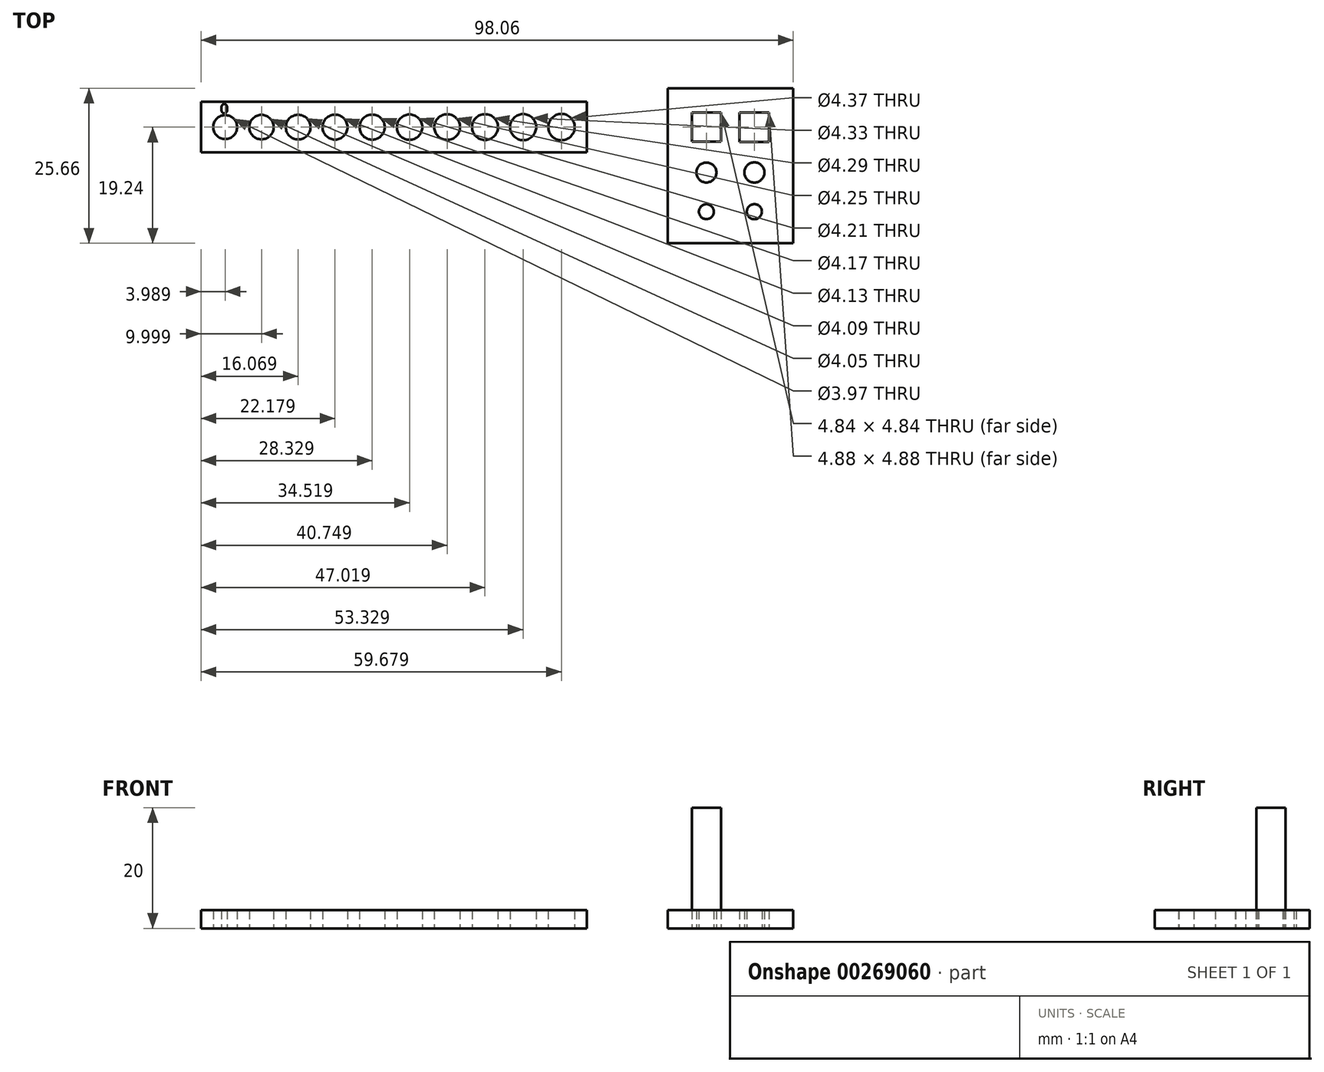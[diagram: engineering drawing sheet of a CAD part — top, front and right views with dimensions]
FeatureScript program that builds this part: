
annotation { "Feature Type Name" : "Feature", "Feature Type Description" : "" }
export const myFeature = defineFeature(function(context is Context, id is Id, definition is map)
    precondition{}
    {
        {
            var Q0;
            Q0=qCreatedBy(makeId("Top.planeOp"),FACE);
            var sketch = newSketch(context, id + "F0", { "sketchPlane" : qUnion([Q0])});
            skLineSegment(sketch, "E0", {"start": v(-79.68, 0) * mm, "end": v(-31, 0) * mm, "construction": true});
            skCircle(sketch, "E1", {"center": v(-79.68, 0) * mm, "radius": 1.99 * mm});
            skCircle(sketch, "E2", {"center": v(-73.67, 0) * mm, "radius": 2.02 * mm});
            skCircle(sketch, "E3", {"center": v(-67.6, 0) * mm, "radius": 2.04 * mm});
            skCircle(sketch, "E4", {"center": v(-61.5, 0) * mm, "radius": 2.06 * mm});
            skCircle(sketch, "E5", {"center": v(-55.34, 0) * mm, "radius": 2.08 * mm});
            skCircle(sketch, "E6", {"center": v(-49.15, 0) * mm, "radius": 2.1 * mm});
            skCircle(sketch, "E7", {"center": v(-42.92, 0) * mm, "radius": 2.12 * mm});
            skCircle(sketch, "E8", {"center": v(-36.65, 0) * mm, "radius": 2.15 * mm});
            skCircle(sketch, "E9", {"center": v(-30.34, 0) * mm, "radius": 2.17 * mm});
            skCircle(sketch, "E10", {"center": v(-24, 0) * mm, "radius": 2.19 * mm});
            skLineSegment(sketch, "E11.bottom", {"start": v(-19.8, -4.19) * mm, "end": v(-83.67, -4.19) * mm});
            skLineSegment(sketch, "E11.top", {"start": v(-19.8, 4.19) * mm, "end": v(-83.67, 4.19) * mm});
            skLineSegment(sketch, "E11.left", {"start": v(-19.8, -4.19) * mm, "end": v(-19.8, 4.19) * mm});
            skLineSegment(sketch, "E11.right", {"start": v(-83.67, -4.19) * mm, "end": v(-83.67, 4.19) * mm});
            skPoint(sketch, "E11.middle", {"position": v(-51.74, 0) * mm});
            skText(sketch, "E12", { "text": "0", "fontName": "OpenSans-Regular.ttf"});
            const initialGuessF0  = {"E12": [-0.08042, 0.0023, 1, 0, 0.0015]};
            skSetInitialGuess(sketch, initialGuessF0);
            skSolve(sketch);
        }
        {
            var Q0;
            Q0=makeQuery(id+"F0.imprint","IMPRINT",FACE,{"disambiguationData":[TD([[makeQuery(id+"F0.imprint","IMPRINT",EDGE,{"derivedFrom":sQuery(id+"F0.wireOp",EDGE,"E1")}),-1.0]])]});
            extrude(context, id + "F1", {"entities" : qUnion([Q0]), "depth" : 3 * mm});
        }
        {
            var Q0;
            Q0=qCreatedBy(makeId("Top.planeOp"),FACE);
            var sketch = newSketch(context, id + "F2", { "sketchPlane" : qUnion([Q0])});
            skLineSegment(sketch, "E13.bottom", {"start": v(2.42, -2.42) * mm, "end": v(-2.42, -2.42) * mm});
            skLineSegment(sketch, "E13.top", {"start": v(2.42, 2.42) * mm, "end": v(-2.42, 2.42) * mm});
            skLineSegment(sketch, "E13.left", {"start": v(2.42, -2.42) * mm, "end": v(2.42, 2.42) * mm});
            skLineSegment(sketch, "E13.right", {"start": v(-2.42, -2.42) * mm, "end": v(-2.42, 2.42) * mm});
            skPoint(sketch, "E13.middle", {"position": v(0, 0) * mm});
            skLineSegment(sketch, "E14.bottom", {"start": v(10.39, -2.44) * mm, "end": v(5.5, -2.44) * mm});
            skLineSegment(sketch, "E14.top", {"start": v(10.39, 2.44) * mm, "end": v(5.5, 2.44) * mm});
            skLineSegment(sketch, "E14.left", {"start": v(10.39, -2.44) * mm, "end": v(10.39, 2.44) * mm});
            skLineSegment(sketch, "E14.right", {"start": v(5.5, -2.44) * mm, "end": v(5.5, 2.44) * mm});
            skPoint(sketch, "E14.middle", {"position": v(7.95, 0) * mm});
            skCircle(sketch, "E15", {"center": v(0, -7.52) * mm, "radius": 1.66 * mm});
            skLineSegment(sketch, "E16", {"start": v(0, -7.52) * mm, "end": v(37.49, -7.52) * mm, "construction": true});
            skCircle(sketch, "E17", {"center": v(7.95, -7.52) * mm, "radius": 1.67 * mm});
            skCircle(sketch, "E18", {"center": v(0, -14) * mm, "radius": 1.24 * mm});
            skLineSegment(sketch, "E19", {"start": v(0, -14) * mm, "end": v(33.84, -14) * mm, "construction": true});
            skCircle(sketch, "E20", {"center": v(7.95, -14) * mm, "radius": 1.25 * mm});
            skLineSegment(sketch, "E21", {"start": v(7.95, 0) * mm, "end": v(7.95, -28.02) * mm, "construction": true});
            skLineSegment(sketch, "E22.bottom", {"start": v(-6.42, 6.42) * mm, "end": v(14.39, 6.42) * mm});
            skLineSegment(sketch, "E22.top", {"start": v(-6.42, -19.24) * mm, "end": v(14.39, -19.24) * mm});
            skLineSegment(sketch, "E22.left", {"start": v(-6.42, 6.42) * mm, "end": v(-6.42, -19.24) * mm});
            skLineSegment(sketch, "E22.right", {"start": v(14.39, 6.42) * mm, "end": v(14.39, -19.24) * mm});
            skSolve(sketch);
        }
        {
            var Q0;
            Q0=makeQuery(id+"F2.imprint","IMPRINT",FACE,{"disambiguationData":[TD([[makeQuery(id+"F2.imprint","IMPRINT",EDGE,{"derivedFrom":sQuery(id+"F2.wireOp",EDGE,"E13.bottom")}),1.0]])]});
            extrude(context, id + "F3", {"entities" : qUnion([Q0]), "depth" : 3 * mm});
        }
        {
            var Q0;
            Q0=makeQuery(id+"F2.imprint","IMPRINT",FACE,{"disambiguationData":[TD([[makeQuery(id+"F2.imprint","IMPRINT",EDGE,{"derivedFrom":sQuery(id+"F2.wireOp",EDGE,"E13.bottom")}),-1.0]])]});
            var Q1;
            Q1=sQuery(id+"F2.wireOp",EDGE,"E13.bottom");
            var Q2;
            Q2=sQuery(id+"F2.wireOp",EDGE,"E13.left");
            var Q3;
            Q3=sQuery(id+"F2.wireOp",EDGE,"E13.top");
            var Q4;
            Q4=sQuery(id+"F2.wireOp",EDGE,"E13.right");
            extrude(context, id + "F4", {"entities" : qUnion([Q0]), "surfaceEntities" : qUnion([Q1, Q2, Q3, Q4]), "depth" : 20 * mm});
        }
    });
